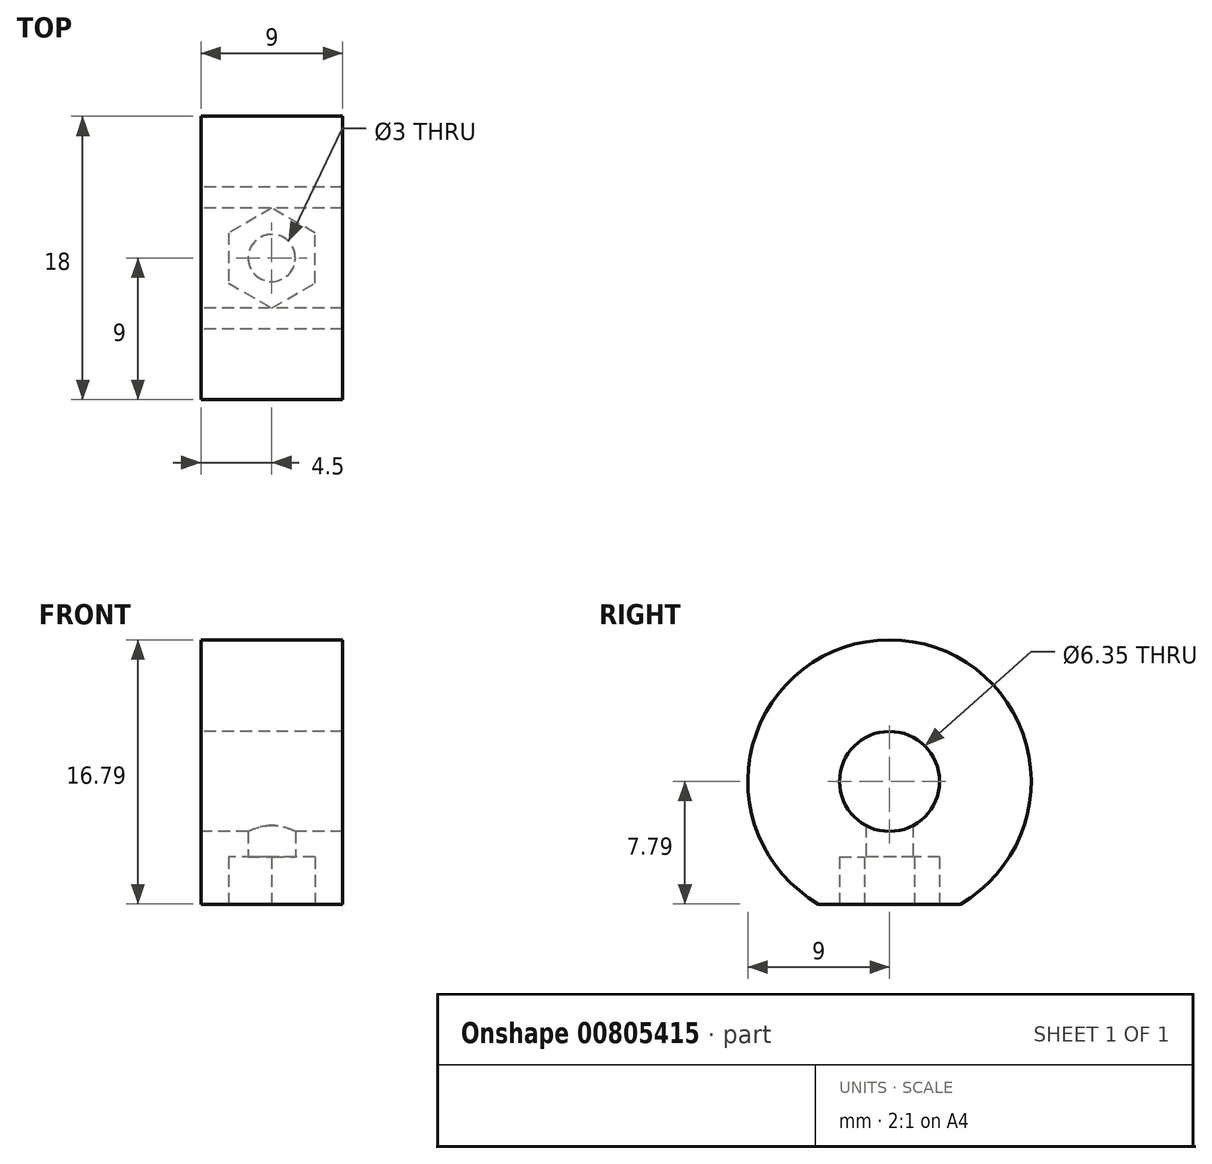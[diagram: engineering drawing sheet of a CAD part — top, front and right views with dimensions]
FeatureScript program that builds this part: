
annotation { "Feature Type Name" : "Feature", "Feature Type Description" : "" }
export const myFeature = defineFeature(function(context is Context, id is Id, definition is map)
    precondition{}
    {
        {
            var Q0;
            Q0=qCreatedBy(makeId("Right.planeOp"),FACE);
            var sketch = newSketch(context, id + "F0", { "sketchPlane" : qUnion([Q0])});
            skCircle(sketch, "E0", {"center": v(0, 0) * mm, "radius": 3.17 * mm});
            skLineSegment(sketch, "E1", {"start": v(-4.5, -7.8) * mm, "end": v(4.5, -7.8) * mm});
            skArc(sketch, "E2", {"start": v(-4.5, -7.8) * mm, "mid": v(0, 9) * mm, "end": v(4.5, -7.8) * mm});
            skSolve(sketch);
        }
        {
            var Q0;
            Q0 = qSketchRegion(id + "F0", true);
            extrude(context, id + "F1", {"entities" : qUnion([Q0]), "depth" : 9 * mm, "offsetDistance" : 25 * mm});
        }
        {
            var Q0;
            Q0=makeQuery(id+"F1.opExtrude","SWEPT_FACE",FACE,{"disambiguationData":[OSD([sQuery(id+"F0.wireOp",EDGE,"E1")])]});
            var sketch = newSketch(context, id + "F2", { "sketchPlane" : qUnion([Q0])});
            skPoint(sketch, "E3", {"position": v(4.5, 4.5) * mm});
            skPoint(sketch, "E4", {"position": v(4.5, -4.5) * mm});
            skLineSegment(sketch, "E5", {"start": v(4.5, 4.5) * mm, "end": v(4.5, -4.5) * mm, "construction": true});
            skCircle(sketch, "E6.cCircle", {"center": v(4.5, 0) * mm, "radius": 2.75 * mm, "construction": true});
            skLineSegment(sketch, "E6.0", {"start": v(1.75, -1.59) * mm, "end": v(1.75, 1.59) * mm});
            skLineSegment(sketch, "E6.1", {"start": v(1.75, 1.59) * mm, "end": v(4.5, 3.18) * mm});
            skLineSegment(sketch, "E6.2", {"start": v(4.5, 3.18) * mm, "end": v(7.25, 1.59) * mm});
            skLineSegment(sketch, "E6.3", {"start": v(7.25, 1.59) * mm, "end": v(7.25, -1.59) * mm});
            skLineSegment(sketch, "E6.4", {"start": v(7.25, -1.59) * mm, "end": v(4.5, -3.18) * mm});
            skLineSegment(sketch, "E6.5", {"start": v(4.5, -3.18) * mm, "end": v(1.75, -1.59) * mm});
            skPoint(sketch, "E6.0.midPoint", {"position": v(1.75, 0) * mm});
            skSolve(sketch);
        }
        {
            var Q0;
            Q0 = qSketchRegion(id + "F2", true);
            extrude(context, id + "F3", {"entities" : qUnion([Q0]), "operationType" : NewBodyOperationType.REMOVE, "oppositeDirection" : true, "depth" : 3 * mm, "offsetDistance" : 25 * mm});
        }
        {
            var Q0;
            Q0=makeQuery(id+"F1.opExtrude","SWEPT_FACE",FACE,{"disambiguationData":[OSD([sQuery(id+"F0.wireOp",EDGE,"E1")])]});
            var sketch = newSketch(context, id + "F4", { "sketchPlane" : qUnion([Q0])});
            skPoint(sketch, "E7", {"position": v(4.5, 4.5) * mm});
            skPoint(sketch, "E8", {"position": v(4.5, -4.5) * mm});
            skLineSegment(sketch, "E9", {"start": v(4.5, 4.5) * mm, "end": v(4.5, -4.5) * mm, "construction": true});
            skCircle(sketch, "E10", {"center": v(4.5, 0) * mm, "radius": 1.5 * mm});
            skSolve(sketch);
        }
        {
            var Q0;
            Q0 = qSketchRegion(id + "F4", true);
            extrude(context, id + "F5", {"entities" : qUnion([Q0]), "operationType" : NewBodyOperationType.REMOVE, "oppositeDirection" : true, "depth" : 6 * mm, "offsetDistance" : 25 * mm});
        }
    });
